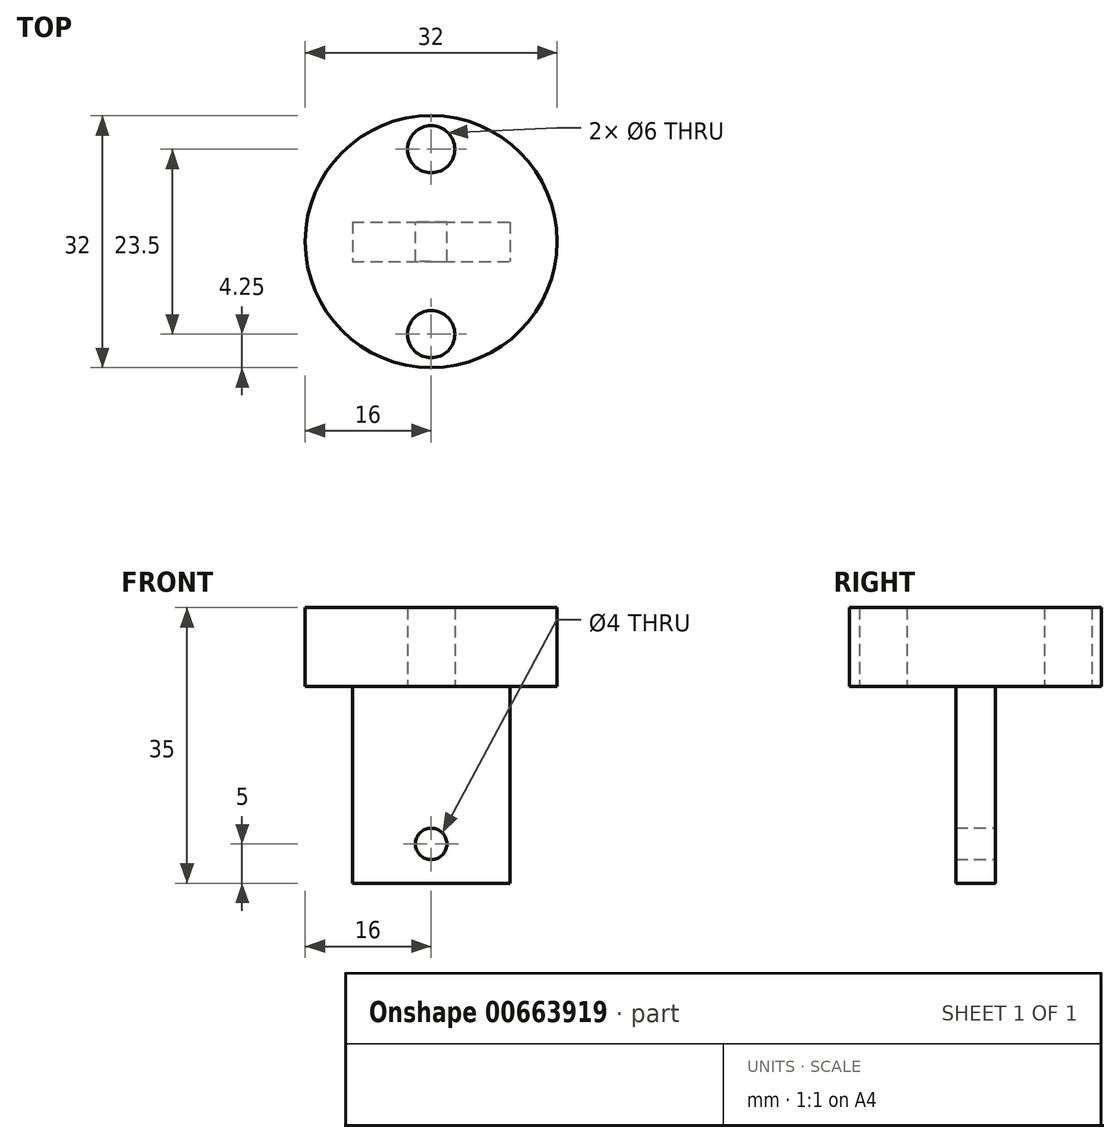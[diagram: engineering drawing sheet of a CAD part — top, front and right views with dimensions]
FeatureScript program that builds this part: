
annotation { "Feature Type Name" : "Feature", "Feature Type Description" : "" }
export const myFeature = defineFeature(function(context is Context, id is Id, definition is map)
    precondition{}
    {
        {
            var Q0;
            Q0=qCreatedBy(makeId("Top.planeOp"),FACE);
            var sketch = newSketch(context, id + "F0", { "sketchPlane" : qUnion([Q0])});
            skCircle(sketch, "E0", {"center": v(0, 0) * mm, "radius": 16 * mm});
            skPoint(sketch, "E1", {"position": v(0, 11.75) * mm});
            skPoint(sketch, "E2", {"position": v(0, -11.75) * mm});
            skCircle(sketch, "E3", {"center": v(0, -11.75) * mm, "radius": 3 * mm});
            skCircle(sketch, "E4", {"center": v(0, 11.75) * mm, "radius": 3 * mm});
            skSolve(sketch);
        }
        {
            var Q0;
            Q0=makeQuery(id+"F0.imprint","IMPRINT",FACE,{"disambiguationData":[TD([[makeQuery(id+"F0.imprint","IMPRINT",EDGE,{"derivedFrom":sQuery(id+"F0.wireOp",EDGE,"E0")}),1.0]])]});
            extrude(context, id + "F1", {"entities" : qUnion([Q0]), "depth" : 10 * mm, "offsetDistance" : 25 * mm});
        }
        {
            var Q0;
            Q0=makeQuery(id+"F1.opExtrude","CAP_FACE",FACE,{"disambiguationData":[OSD([sQuery(id+"F0.wireOp",EDGE,"E0"),sQuery(id+"F0.wireOp",EDGE,"E3"),sQuery(id+"F0.wireOp",EDGE,"E4")])],"isStart":true});
            var sketch = newSketch(context, id + "F2", { "sketchPlane" : qUnion([Q0])});
            skLineSegment(sketch, "E5.bottom", {"start": v(-10, 2.5) * mm, "end": v(10, 2.5) * mm});
            skLineSegment(sketch, "E5.top", {"start": v(-10, -2.5) * mm, "end": v(10, -2.5) * mm});
            skLineSegment(sketch, "E5.left", {"start": v(-10, -2.5) * mm, "end": v(-10, 2.5) * mm});
            skLineSegment(sketch, "E5.right", {"start": v(10, -2.5) * mm, "end": v(10, 2.5) * mm});
            skSolve(sketch);
        }
        {
            var Q0;
            Q0=makeQuery(id+"F2.imprint","IMPRINT",FACE,{"disambiguationData":[TD([[makeQuery(id+"F2.imprint","IMPRINT",EDGE,{"derivedFrom":sQuery(id+"F2.wireOp",EDGE,"E5.bottom")}),-1.0]])]});
            extrude(context, id + "F3", {"entities" : qUnion([Q0]), "operationType" : NewBodyOperationType.ADD, "depth" : 25 * mm, "offsetDistance" : 25 * mm});
        }
        {
            var Q0;
            Q0=makeQuery(id+"F3.opExtrude","SWEPT_FACE",FACE,{"disambiguationData":[OSD([sQuery(id+"F2.wireOp",EDGE,"E5.top")])]});
            var sketch = newSketch(context, id + "F4", { "sketchPlane" : qUnion([Q0])});
            skPoint(sketch, "E6", {"position": v(0, -20) * mm});
            skSolve(sketch);
        }
        {
            var Q0;
            Q0=sQuery(id+"F4.wireOp",VERTEX,"E6");
            var Q1;
            Q1=makeQuery(id+"F1.opExtrude","SWEPT_BODY",BODY,{"disambiguationData":[OSD([sQuery(id+"F0.wireOp",EDGE,"E0"),sQuery(id+"F0.wireOp",EDGE,"E3"),sQuery(id+"F0.wireOp",EDGE,"E4")])]});
            hole(context, id + "F5", {"style" : HoleStyle.SIMPLE, "endStyle" : HoleEndStyle.THROUGH, "holeDiameter" : 4 * mm, "majorDiameter" : 5 * mm, "isTappedThrough" : true, "tappedDepth" : 12 * mm, "tapClearance" : 3, "locations" : qUnion([Q0]), "scope" : qUnion([Q1])});
        }
    });
